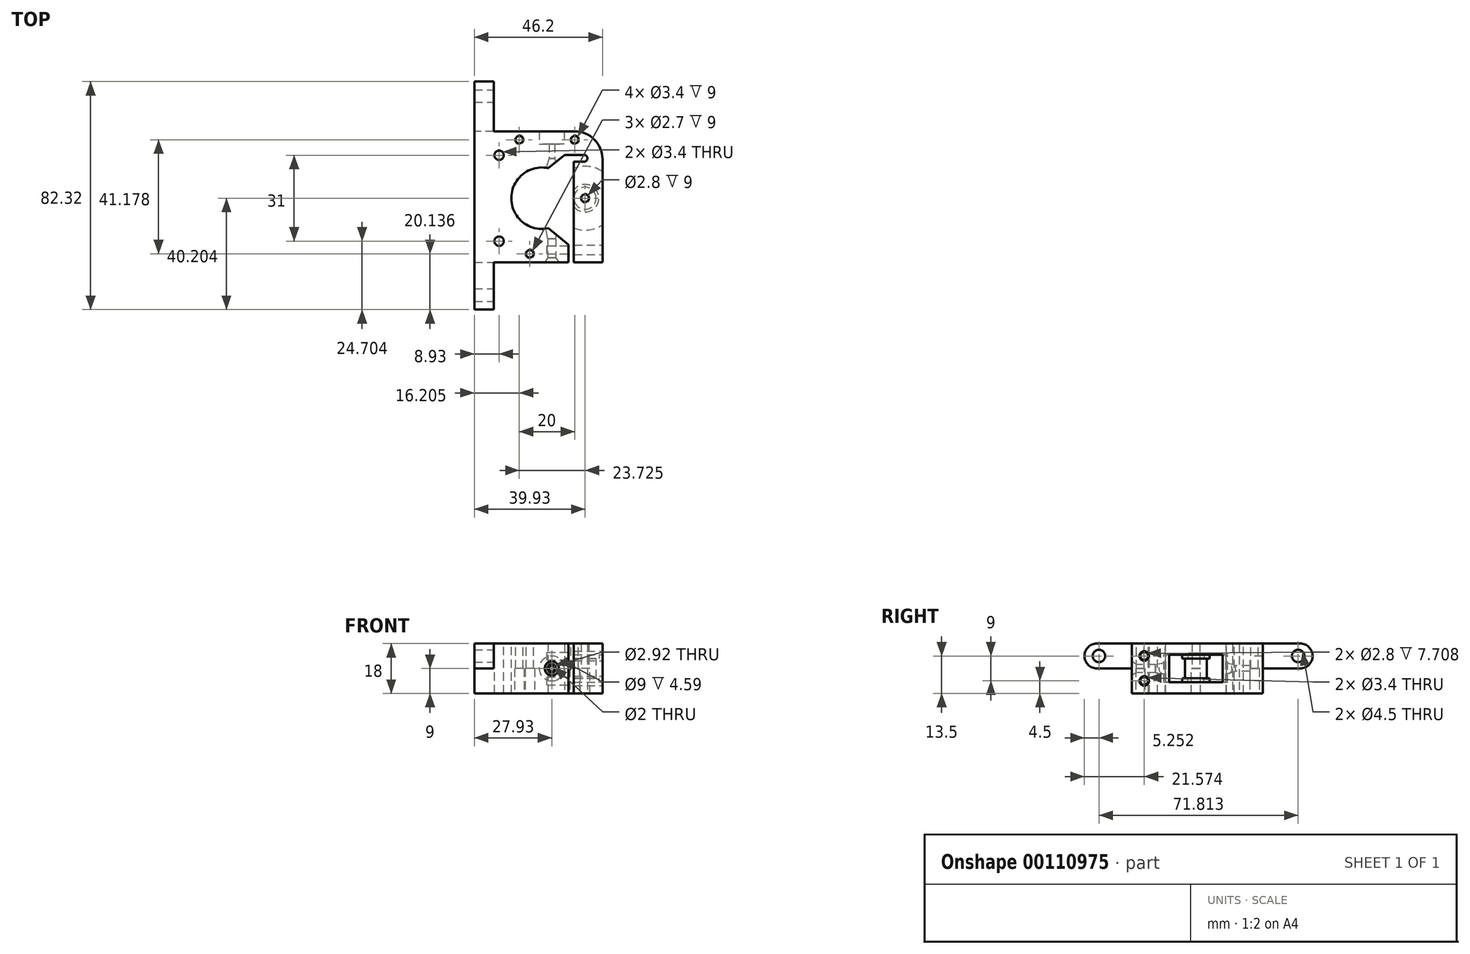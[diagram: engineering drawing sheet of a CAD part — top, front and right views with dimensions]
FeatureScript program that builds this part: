
annotation { "Feature Type Name" : "Feature", "Feature Type Description" : "" }
export const myFeature = defineFeature(function(context is Context, id is Id, definition is map)
    precondition{}
    {
        {
            var Q0;
            Q0=qCreatedBy(makeId("Top.planeOp"),FACE);
            var sketch = newSketch(context, id + "F0", { "sketchPlane" : qUnion([Q0])});
            skLineSegment(sketch, "E0", {"start": v(-24.43, 29.94) * mm, "end": v(-24.43, -17.36) * mm});
            skLineSegment(sketch, "E1", {"start": v(-24.43, -17.36) * mm, "end": v(-24.43, -17.36) * mm});
            skLineSegment(sketch, "E2", {"start": v(-24.43, -17.36) * mm, "end": v(-24.43, -17.35) * mm});
            skLineSegment(sketch, "E3", {"start": v(-24.43, -17.35) * mm, "end": v(9.48, -17.35) * mm});
            skLineSegment(sketch, "E4", {"start": v(9.48, -17.35) * mm, "end": v(9.48, 21.46) * mm});
            skLineSegment(sketch, "E5", {"start": v(9.48, 21.46) * mm, "end": v(15.14, 21.46) * mm});
            skLineSegment(sketch, "E6", {"start": v(15.14, 19) * mm, "end": v(11.48, 19) * mm});
            skLineSegment(sketch, "E7", {"start": v(11.48, 19) * mm, "end": v(11.48, -17.35) * mm});
            skLineSegment(sketch, "E8", {"start": v(11.48, -17.35) * mm, "end": v(21.77, -17.35) * mm});
            skLineSegment(sketch, "E9", {"start": v(21.77, -17.35) * mm, "end": v(21.77, 29.94) * mm});
            skLineSegment(sketch, "E10", {"start": v(21.77, 29.94) * mm, "end": v(-24.43, 29.94) * mm});
            skCircle(sketch, "E11", {"center": v(-8.23, 26.93) * mm, "radius": 1.35 * mm});
            skCircle(sketch, "E12", {"center": v(11.77, 26.93) * mm, "radius": 1.35 * mm});
            skCircle(sketch, "E13", {"center": v(-4.43, -14.24) * mm, "radius": 1.35 * mm});
            skArc(sketch, "E14", {"start": v(15.14, 19) * mm, "mid": v(16.36, 20.23) * mm, "end": v(15.14, 21.46) * mm});
            skCircle(sketch, "E15", {"center": v(-8.23, 26.93) * mm, "radius": 1.7 * mm});
            skCircle(sketch, "E16", {"center": v(11.77, 26.93) * mm, "radius": 1.7 * mm});
            skCircle(sketch, "E17", {"center": v(-4.43, -14.24) * mm, "radius": 1.7 * mm});
            skSolve(sketch);
        }
        {
            var Q0;
            Q0=makeQuery(id+"F0.imprint","IMPRINT",FACE,{"disambiguationData":[TD([[makeQuery(id+"F0.imprint","IMPRINT",EDGE,{"derivedFrom":sQuery(id+"F0.wireOp",EDGE,"E0")}),1.0]])]});
            extrude(context, id + "F1", {"entities" : qUnion([Q0]), "depth" : 9 * mm});
        }
        {
            var Q0;
            Q0=makeQuery(id+"F1.opExtrude","CAP_FACE",FACE,{"disambiguationData":[OSD([sQuery(id+"F0.wireOp",EDGE,"E0"),sQuery(id+"F0.wireOp",EDGE,"E1"),sQuery(id+"F0.wireOp",EDGE,"E2"),sQuery(id+"F0.wireOp",EDGE,"E3"),sQuery(id+"F0.wireOp",EDGE,"E4"),sQuery(id+"F0.wireOp",EDGE,"E5"),sQuery(id+"F0.wireOp",EDGE,"E6"),sQuery(id+"F0.wireOp",EDGE,"E7"),sQuery(id+"F0.wireOp",EDGE,"E8"),sQuery(id+"F0.wireOp",EDGE,"E9"),sQuery(id+"F0.wireOp",EDGE,"E10"),sQuery(id+"F0.wireOp",EDGE,"604cad85-587a-4b7d-8070-06f4cba85480"),sQuery(id+"F0.wireOp",EDGE,"6e5e38c1-5bff-4efe-a8c5-b84022f0a049"),sQuery(id+"F0.wireOp",EDGE,"b8144507-9dd7-4af4-87a3-7b649dd00ae6"),sQuery(id+"F0.wireOp",EDGE,"b9c2cb7c-5e58-4995-888e-a78f0403fbb5"),sQuery(id+"F0.wireOp",EDGE,"885990ab-7576-4c23-8475-595d2769e284"),sQuery(id+"F0.wireOp",EDGE,"E11"),sQuery(id+"F0.wireOp",EDGE,"E12"),sQuery(id+"F0.wireOp",EDGE,"E13"),sQuery(id+"F0.wireOp",EDGE,"E14")])],"isStart":false});
            var sketch = newSketch(context, id + "F2", { "sketchPlane" : qUnion([Q0])});
            skCircle(sketch, "E18", {"center": v(0, 5.82) * mm, "radius": 11.1 * mm});
            skCircle(sketch, "E19", {"center": v(-15.5, 21.32) * mm, "radius": 1.7 * mm});
            skCircle(sketch, "E20", {"center": v(-15.5, -9.68) * mm, "radius": 1.7 * mm});
            skSolve(sketch);
        }
        {
            var Q0;
            Q0=qSketchRegion(id+"F2",true);
            extrude(context, id + "F3", {"entities" : qUnion([Q0]), "operationType" : NewBodyOperationType.REMOVE, "endBound" : BoundingType.THROUGH_ALL, "oppositeDirection" : true, "depth" : 25 * mm});
        }
        {
            var Q0;
            Q0=makeQuery(id+"F1.opExtrude","CAP_FACE",FACE,{"disambiguationData":[OSD([sQuery(id+"F0.wireOp",EDGE,"E0"),sQuery(id+"F0.wireOp",EDGE,"E1"),sQuery(id+"F0.wireOp",EDGE,"E2"),sQuery(id+"F0.wireOp",EDGE,"E3"),sQuery(id+"F0.wireOp",EDGE,"E4"),sQuery(id+"F0.wireOp",EDGE,"E5"),sQuery(id+"F0.wireOp",EDGE,"E6"),sQuery(id+"F0.wireOp",EDGE,"E7"),sQuery(id+"F0.wireOp",EDGE,"E8"),sQuery(id+"F0.wireOp",EDGE,"E9"),sQuery(id+"F0.wireOp",EDGE,"E10"),sQuery(id+"F0.wireOp",EDGE,"604cad85-587a-4b7d-8070-06f4cba85480"),sQuery(id+"F0.wireOp",EDGE,"6e5e38c1-5bff-4efe-a8c5-b84022f0a049"),sQuery(id+"F0.wireOp",EDGE,"E11"),sQuery(id+"F0.wireOp",EDGE,"E12"),sQuery(id+"F0.wireOp",EDGE,"E13"),sQuery(id+"F0.wireOp",EDGE,"E14")])],"isStart":false});
            var sketch = newSketch(context, id + "F4", { "sketchPlane" : qUnion([Q0])});
            skCircle(sketch, "E21", {"center": v(15.5, 5.82) * mm, "radius": 11.5 * mm});
            skCircle(sketch, "E22", {"center": v(15.5, 5.82) * mm, "radius": 5 * mm});
            skCircle(sketch, "E23", {"center": v(15.5, 5.82) * mm, "radius": 4 * mm});
            skLineSegment(sketch, "E24", {"start": v(0, 5.82) * mm, "end": v(31, 5.82) * mm, "construction": true});
            skCircle(sketch, "E25", {"center": v(15.5, 5.82) * mm, "radius": 1.4 * mm});
            skCircle(sketch, "E26", {"center": v(15.5, 5.82) * mm, "radius": 1.7 * mm});
            skSolve(sketch);
        }
        {
            var Q0;
            Q0=makeQuery(id+"F4.imprint","IMPRINT",FACE,{"disambiguationData":[TD([[makeQuery(id+"F4.imprint","IMPRINT",EDGE,{"derivedFrom":sQuery(id+"F4.wireOp",EDGE,"E22")}),-1.0]])]});
            extrude(context, id + "F5", {"entities" : qUnion([Q0]), "operationType" : NewBodyOperationType.REMOVE, "oppositeDirection" : true, "depth" : 5 * mm});
        }
        {
            var Q0;
            Q0=makeQuery(id+"F4.imprint","IMPRINT",FACE,{"disambiguationData":[TD([[makeQuery(id+"F4.imprint","IMPRINT",EDGE,{"derivedFrom":sQuery(id+"F4.wireOp",EDGE,"E22")}),1.0]])]});
            var Q1;
            Q1=makeQuery(id+"F4.imprint","IMPRINT",FACE,{"disambiguationData":[TD([[makeQuery(id+"F4.imprint","IMPRINT",EDGE,{"derivedFrom":sQuery(id+"F4.wireOp",EDGE,"E23")}),-1.0]])]});
            extrude(context, id + "F6", {"entities" : qUnion([Q0, Q1]), "operationType" : NewBodyOperationType.REMOVE, "oppositeDirection" : true, "depth" : 3.5 * mm});
        }
        {
            var Q0;
            {var subQ0=sQuery(id+"F0.wireOp",EDGE,"E0");var subQ1=sQuery(id+"F0.wireOp",EDGE,"E1");var subQ2=sQuery(id+"F0.wireOp",EDGE,"E2");var subQ3=sQuery(id+"F0.wireOp",EDGE,"E3");var subQ4=sQuery(id+"F0.wireOp",EDGE,"E4");var subQ5=sQuery(id+"F0.wireOp",EDGE,"E5");var subQ6=sQuery(id+"F0.wireOp",EDGE,"E6");var subQ7=sQuery(id+"F0.wireOp",EDGE,"E7");var subQ8=sQuery(id+"F0.wireOp",EDGE,"E9");var subQ9=sQuery(id+"F0.wireOp",EDGE,"E10");var subQ10=sQuery(id+"F0.wireOp",EDGE,"604cad85-587a-4b7d-8070-06f4cba85480");var subQ11=sQuery(id+"F0.wireOp",EDGE,"6e5e38c1-5bff-4efe-a8c5-b84022f0a049");var subQ12=sQuery(id+"F0.wireOp",EDGE,"E11");var subQ13=sQuery(id+"F0.wireOp",EDGE,"E12");var subQ14=sQuery(id+"F0.wireOp",EDGE,"E13");var subQ15=sQuery(id+"F0.wireOp",EDGE,"E14");Q0=makeQuery(id+"F5.boolean.opBoolean","SPLIT",FACE,{"disambiguationData":[TD([makeQuery(id+"F1.opExtrude","SWEPT_FACE",FACE,{"disambiguationData":[OSD([subQ0])]})])],"derivedFrom":makeQuery(id+"F1.opExtrude","CAP_FACE",FACE,{"disambiguationData":[OSD([subQ0,subQ1,subQ2,subQ3,subQ4,subQ5,subQ6,subQ7,sQuery(id+"F0.wireOp",EDGE,"E8"),subQ8,subQ9,subQ10,subQ11,subQ12,subQ13,subQ14,subQ15])],"isStart":false})});}
            var sketch = newSketch(context, id + "F7", { "sketchPlane" : qUnion([Q0])});
            skLineSegment(sketch, "E27", {"start": v(-1, 30.34) * mm, "end": v(-1, 25.34) * mm});
            skLineSegment(sketch, "E28", {"start": v(-1, 25.34) * mm, "end": v(2.5, 25.34) * mm});
            skLineSegment(sketch, "E29", {"start": v(2.5, 25.34) * mm, "end": v(2.5, 20.21) * mm});
            skLineSegment(sketch, "E30", {"start": v(2.5, 20.21) * mm, "end": v(0.95, 15.18) * mm});
            skLineSegment(sketch, "E31", {"start": v(0.95, 15.18) * mm, "end": v(3.5, 15.18) * mm});
            skLineSegment(sketch, "E32", {"start": v(3.5, 15.18) * mm, "end": v(3.5, 30.34) * mm});
            skLineSegment(sketch, "E33", {"start": v(3.5, 30.34) * mm, "end": v(-1, 30.34) * mm});
            skLineSegment(sketch, "E34", {"start": v(3.5, -3.13) * mm, "end": v(3.5, -17.35) * mm});
            skLineSegment(sketch, "E35", {"start": v(0.95, -3.15) * mm, "end": v(2.04, -8.75) * mm});
            skLineSegment(sketch, "E36", {"start": v(2.04, -8.75) * mm, "end": v(2.04, -15.66) * mm});
            skLineSegment(sketch, "E37", {"start": v(2.04, -15.66) * mm, "end": v(0.95, -17.35) * mm});
            skLineSegment(sketch, "E38", {"start": v(0.95, -3.15) * mm, "end": v(3.5, -3.13) * mm});
            skSolve(sketch);
        }
        {
            var Q0;
            Q0=qSketchRegion(id+"F7",true);
            var Q1;
            {var subQ1=sQuery(id+"F7.wireOp",EDGE,"E34");Q1=makeQuery(id+"F7.imprint","IMPRINT",FACE,{"disambiguationData":[TD([[makeQuery(id+"F7.imprint","IMPRINT",EDGE,{"derivedFrom":subQ1}),-1.0]])]});}
            var Q2;
            {var subQ0=sQuery(id+"F7.wireOp",EDGE,"E38");Q2=makeQuery(id+"F7.imprint","IMPRINT",FACE,{"disambiguationData":[TD([[makeQuery(id+"F7.imprint","IMPRINT",EDGE,{"derivedFrom":subQ0}),-1.0]])]});}
            var Q3;
            {var subQ6=sQuery(id+"F7.wireOp",EDGE,"E36");Q3=makeQuery(id+"F7.imprint","IMPRINT",FACE,{"disambiguationData":[TD([[makeQuery(id+"F7.imprint","IMPRINT",EDGE,{"derivedFrom":subQ6}),1.0]])]});}
            var Q4;
            Q4=sQuery(id+"F7.wireOp",EDGE,"E32");
            revolve(context, id + "F8", {"entities" : qUnion([Q0, Q1, Q2, Q3]), "axis" : qUnion([Q4]), "revolveType" : RevolveType.FULL});
        }
        {
            var Q0;
            Q0=makeQuery(id+"F8.opRevolve","SWEPT_BODY",BODY,{"disambiguationData":[OSD([sQuery(id+"F7.wireOp",EDGE,"E27"),sQuery(id+"F7.wireOp",EDGE,"E28"),sQuery(id+"F7.wireOp",EDGE,"E29"),sQuery(id+"F7.wireOp",EDGE,"E30"),sQuery(id+"F7.wireOp",EDGE,"E31"),sQuery(id+"F7.wireOp",EDGE,"E32"),sQuery(id+"F7.wireOp",EDGE,"E33")])]});
            var Q1;
            Q1=makeQuery(id+"F8.opRevolve","SWEPT_BODY",BODY,{"disambiguationData":[OSD([sQuery(id+"F0.wireOp",EDGE,"E3"),sQuery(id+"F7.wireOp",EDGE,"E34"),sQuery(id+"F7.wireOp",EDGE,"E35"),sQuery(id+"F7.wireOp",EDGE,"E36"),sQuery(id+"F7.wireOp",EDGE,"E37"),sQuery(id+"F7.wireOp",EDGE,"E38")])]});
            var Q2;
            Q2=makeQuery(id+"F1.opExtrude","SWEPT_BODY",BODY,{"disambiguationData":[OSD([sQuery(id+"F0.wireOp",EDGE,"E0"),sQuery(id+"F0.wireOp",EDGE,"E1"),sQuery(id+"F0.wireOp",EDGE,"E2"),sQuery(id+"F0.wireOp",EDGE,"E3"),sQuery(id+"F0.wireOp",EDGE,"E4"),sQuery(id+"F0.wireOp",EDGE,"E5"),sQuery(id+"F0.wireOp",EDGE,"E6"),sQuery(id+"F0.wireOp",EDGE,"E7"),sQuery(id+"F0.wireOp",EDGE,"E8"),sQuery(id+"F0.wireOp",EDGE,"E9"),sQuery(id+"F0.wireOp",EDGE,"E10"),sQuery(id+"F0.wireOp",EDGE,"604cad85-587a-4b7d-8070-06f4cba85480"),sQuery(id+"F0.wireOp",EDGE,"6e5e38c1-5bff-4efe-a8c5-b84022f0a049"),sQuery(id+"F0.wireOp",EDGE,"E11"),sQuery(id+"F0.wireOp",EDGE,"E12"),sQuery(id+"F0.wireOp",EDGE,"E13"),sQuery(id+"F0.wireOp",EDGE,"E14")])]});
            booleanBodies(context, id + "F9", {"operationType" : BooleanOperationType.SUBTRACTION, "tools" : qUnion([Q0, Q1]), "targets" : qUnion([Q2]), "keepTools" : true});
        }
        {
            var Q0;
            Q0=makeQuery(id+"F8.opRevolve","SWEPT_BODY",BODY,{"disambiguationData":[OSD([sQuery(id+"F7.wireOp",EDGE,"E27"),sQuery(id+"F7.wireOp",EDGE,"E28"),sQuery(id+"F7.wireOp",EDGE,"E29"),sQuery(id+"F7.wireOp",EDGE,"E30"),sQuery(id+"F7.wireOp",EDGE,"E31"),sQuery(id+"F7.wireOp",EDGE,"E32"),sQuery(id+"F7.wireOp",EDGE,"E33")])]});
            var Q1;
            Q1=makeQuery(id+"F8.opRevolve","SWEPT_BODY",BODY,{"disambiguationData":[OSD([sQuery(id+"F0.wireOp",EDGE,"E3"),sQuery(id+"F7.wireOp",EDGE,"E34"),sQuery(id+"F7.wireOp",EDGE,"E35"),sQuery(id+"F7.wireOp",EDGE,"E36"),sQuery(id+"F7.wireOp",EDGE,"E37"),sQuery(id+"F7.wireOp",EDGE,"E38")])]});
            var Q2;
            Q2=makeQuery(id+"F1.opExtrude","SWEPT_BODY",BODY,{"disambiguationData":[OSD([sQuery(id+"F0.wireOp",EDGE,"E0"),sQuery(id+"F0.wireOp",EDGE,"E1"),sQuery(id+"F0.wireOp",EDGE,"E2"),sQuery(id+"F0.wireOp",EDGE,"E3"),sQuery(id+"F0.wireOp",EDGE,"E4"),sQuery(id+"F0.wireOp",EDGE,"E5"),sQuery(id+"F0.wireOp",EDGE,"E6"),sQuery(id+"F0.wireOp",EDGE,"E7"),sQuery(id+"F0.wireOp",EDGE,"E8"),sQuery(id+"F0.wireOp",EDGE,"E9"),sQuery(id+"F0.wireOp",EDGE,"E10"),sQuery(id+"F0.wireOp",EDGE,"604cad85-587a-4b7d-8070-06f4cba85480"),sQuery(id+"F0.wireOp",EDGE,"6e5e38c1-5bff-4efe-a8c5-b84022f0a049"),sQuery(id+"F0.wireOp",EDGE,"E11"),sQuery(id+"F0.wireOp",EDGE,"E12"),sQuery(id+"F0.wireOp",EDGE,"E13"),sQuery(id+"F0.wireOp",EDGE,"E14")])]});
            booleanBodies(context, id + "F10", {"operationType" : BooleanOperationType.SUBTRACTION, "tools" : qUnion([Q0, Q1]), "targets" : qUnion([Q2]), "keepTools" : true});
        }
        {
            var Q0;
            Q0=makeQuery(id+"F1.opExtrude","SWEPT_EDGE",EDGE,{"disambiguationData":[OSD([sQuery(id+"F0.wireOp",EDGE,"E9"),sQuery(id+"F0.wireOp",EDGE,"E10")])]});
            fillet(context, id + "F11", {"entities" : qUnion([Q0]), "radius" : 10 * mm, "tangentPropagation" : true, "allowEdgeOverflow" : false});
        }
        {
            var Q0;
            Q0=qSketchRegion(id+"F0",true);
            var Q1;
            Q1=makeQuery(id+"F0.imprint","IMPRINT",FACE,{"disambiguationData":[TD([[makeQuery(id+"F0.imprint","IMPRINT",EDGE,{"derivedFrom":sQuery(id+"F0.wireOp",EDGE,"E12")}),-1.0]])]});
            var Q2;
            Q2=makeQuery(id+"F0.imprint","IMPRINT",FACE,{"disambiguationData":[TD([[makeQuery(id+"F0.imprint","IMPRINT",EDGE,{"derivedFrom":sQuery(id+"F0.wireOp",EDGE,"E11")}),-1.0]])]});
            var Q3;
            Q3=makeQuery(id+"F0.imprint","IMPRINT",FACE,{"disambiguationData":[TD([[makeQuery(id+"F0.imprint","IMPRINT",EDGE,{"derivedFrom":sQuery(id+"F0.wireOp",EDGE,"E13")}),-1.0]])]});
            extrude(context, id + "F12", {"entities" : qUnion([Q0, Q1, Q2, Q3]), "oppositeDirection" : true, "depth" : 9 * mm});
        }
        {
            var Q0;
            Q0=makeQuery(id+"F12.opExtrude","SWEPT_BODY",BODY,{"disambiguationData":[OSD([sQuery(id+"F0.wireOp",EDGE,"E0"),sQuery(id+"F0.wireOp",EDGE,"E3"),sQuery(id+"F0.wireOp",EDGE,"E4"),sQuery(id+"F0.wireOp",EDGE,"E5"),sQuery(id+"F0.wireOp",EDGE,"E6"),sQuery(id+"F0.wireOp",EDGE,"E7"),sQuery(id+"F0.wireOp",EDGE,"E8"),sQuery(id+"F0.wireOp",EDGE,"E9"),sQuery(id+"F0.wireOp",EDGE,"E10"),sQuery(id+"F0.wireOp",EDGE,"E11"),sQuery(id+"F0.wireOp",EDGE,"E12"),sQuery(id+"F0.wireOp",EDGE,"E13"),sQuery(id+"F0.wireOp",EDGE,"E14")])]});
            transform(context, id + "F13", {"entities" : qUnion([Q0]), "transformType" : TransformType.TRANSLATION_3D, "dx" : 0 * mm, "dy" : 0 * mm, "dz" : 18 * mm, "makeCopy" : false});
        }
        {
            var Q0;
            Q0=makeQuery(id+"F12.opExtrude","SWEPT_EDGE",EDGE,{"disambiguationData":[OSD([sQuery(id+"F0.wireOp",EDGE,"E9"),sQuery(id+"F0.wireOp",EDGE,"E10")])]});
            fillet(context, id + "F14", {"entities" : qUnion([Q0]), "radius" : 10 * mm, "tangentPropagation" : true, "allowEdgeOverflow" : false});
        }
        {
            var Q0;
            Q0=qSketchRegion(id+"F2",true);
            extrude(context, id + "F15", {"entities" : qUnion([Q0]), "operationType" : NewBodyOperationType.REMOVE, "endBound" : BoundingType.THROUGH_ALL, "depth" : 25 * mm});
        }
        {
            var Q0;
            {var subQ3=sQuery(id+"F4.wireOp",EDGE,"E21");var subQ7=makeQuery(id+"F1.opExtrude","CAP_EDGE",EDGE,{"disambiguationData":[OSD([sQuery(id+"F0.wireOp",EDGE,"E9")])],"isStart":false});var subQ9=makeQuery(id+"F4.imprint","INTERSECT",VERTEX,{"disambiguationData":[OD(0.0)],"derivedFrom":[subQ7,subQ3]});Q0=makeQuery(id+"F4.imprint","IMPRINT",FACE,{"disambiguationData":[TD([[makeQuery(id+"F4.imprint","IMPRINT",EDGE,{"disambiguationData":[TD([[subQ9,-1.0]])],"derivedFrom":subQ3}),1.0]])]});}
            extrude(context, id + "F16", {"entities" : qUnion([Q0]), "operationType" : NewBodyOperationType.REMOVE, "depth" : 5 * mm});
        }
        {
            var Q0;
            Q0=makeQuery(id+"F4.imprint","IMPRINT",FACE,{"disambiguationData":[TD([[makeQuery(id+"F4.imprint","IMPRINT",EDGE,{"derivedFrom":sQuery(id+"F4.wireOp",EDGE,"E23")}),-1.0]])]});
            extrude(context, id + "F17", {"entities" : qUnion([Q0]), "operationType" : NewBodyOperationType.REMOVE, "depth" : 3.5 * mm});
        }
        {
            var Q0;
            Q0=makeQuery(id+"F8.opRevolve","SWEPT_BODY",BODY,{"disambiguationData":[OSD([sQuery(id+"F7.wireOp",EDGE,"E27"),sQuery(id+"F7.wireOp",EDGE,"E28"),sQuery(id+"F7.wireOp",EDGE,"E29"),sQuery(id+"F7.wireOp",EDGE,"E30"),sQuery(id+"F7.wireOp",EDGE,"E31"),sQuery(id+"F7.wireOp",EDGE,"E32"),sQuery(id+"F7.wireOp",EDGE,"E33")])]});
            var Q1;
            Q1=makeQuery(id+"F12.opExtrude","SWEPT_BODY",BODY,{"disambiguationData":[OSD([sQuery(id+"F0.wireOp",EDGE,"E0"),sQuery(id+"F0.wireOp",EDGE,"E3"),sQuery(id+"F0.wireOp",EDGE,"E4"),sQuery(id+"F0.wireOp",EDGE,"E5"),sQuery(id+"F0.wireOp",EDGE,"E6"),sQuery(id+"F0.wireOp",EDGE,"E7"),sQuery(id+"F0.wireOp",EDGE,"E8"),sQuery(id+"F0.wireOp",EDGE,"E9"),sQuery(id+"F0.wireOp",EDGE,"E10"),sQuery(id+"F0.wireOp",EDGE,"E11"),sQuery(id+"F0.wireOp",EDGE,"E12"),sQuery(id+"F0.wireOp",EDGE,"E13"),sQuery(id+"F0.wireOp",EDGE,"E14")])]});
            booleanBodies(context, id + "F18", {"operationType" : BooleanOperationType.SUBTRACTION, "tools" : qUnion([Q0]), "targets" : qUnion([Q1])});
        }
        {
            var Q0;
            Q0=makeQuery(id+"F8.opRevolve","SWEPT_BODY",BODY,{"disambiguationData":[OSD([sQuery(id+"F0.wireOp",EDGE,"E3"),sQuery(id+"F7.wireOp",EDGE,"E34"),sQuery(id+"F7.wireOp",EDGE,"E35"),sQuery(id+"F7.wireOp",EDGE,"E36"),sQuery(id+"F7.wireOp",EDGE,"E37"),sQuery(id+"F7.wireOp",EDGE,"E38")])]});
            var Q1;
            Q1=makeQuery(id+"F12.opExtrude","SWEPT_BODY",BODY,{"disambiguationData":[OSD([sQuery(id+"F0.wireOp",EDGE,"E0"),sQuery(id+"F0.wireOp",EDGE,"E3"),sQuery(id+"F0.wireOp",EDGE,"E4"),sQuery(id+"F0.wireOp",EDGE,"E5"),sQuery(id+"F0.wireOp",EDGE,"E6"),sQuery(id+"F0.wireOp",EDGE,"E7"),sQuery(id+"F0.wireOp",EDGE,"E8"),sQuery(id+"F0.wireOp",EDGE,"E9"),sQuery(id+"F0.wireOp",EDGE,"E10"),sQuery(id+"F0.wireOp",EDGE,"E11"),sQuery(id+"F0.wireOp",EDGE,"E12"),sQuery(id+"F0.wireOp",EDGE,"E13"),sQuery(id+"F0.wireOp",EDGE,"E14")])]});
            booleanBodies(context, id + "F19", {"operationType" : BooleanOperationType.SUBTRACTION, "tools" : qUnion([Q0]), "targets" : qUnion([Q1])});
        }
        {
            var Q0;
            Q0=makeQuery(id+"F12.opExtrude","SWEPT_FACE",FACE,{"disambiguationData":[OSD([sQuery(id+"F0.wireOp",EDGE,"E9")])]});
            var sketch = newSketch(context, id + "F20", { "sketchPlane" : qUnion([Q0])});
            skCircle(sketch, "E39", {"center": v(-12.8, 13.5) * mm, "radius": 1.7 * mm});
            skCircle(sketch, "E40", {"center": v(-12.8, 13.5) * mm, "radius": 1.4 * mm});
            skCircle(sketch, "E41", {"center": v(-12.8, 4.5) * mm, "radius": 1.7 * mm});
            skCircle(sketch, "E42", {"center": v(-12.8, 4.5) * mm, "radius": 1.4 * mm});
            skSolve(sketch);
        }
        {
            var Q0;
            Q0=makeQuery(id+"F20.imprint","IMPRINT",FACE,{"disambiguationData":[TD([[makeQuery(id+"F20.imprint","IMPRINT",EDGE,{"derivedFrom":sQuery(id+"F20.wireOp",EDGE,"E40")}),1.0]])]});
            extrude(context, id + "F21", {"entities" : qUnion([Q0]), "operationType" : NewBodyOperationType.REMOVE, "oppositeDirection" : true, "depth" : 20 * mm});
        }
        {
            var Q0;
            Q0=makeQuery(id+"F20.imprint","IMPRINT",FACE,{"disambiguationData":[TD([[makeQuery(id+"F20.imprint","IMPRINT",EDGE,{"derivedFrom":sQuery(id+"F20.wireOp",EDGE,"E39")}),1.0]])]});
            extrude(context, id + "F22", {"entities" : qUnion([Q0]), "operationType" : NewBodyOperationType.REMOVE, "oppositeDirection" : true, "depth" : 11 * mm});
        }
        {
            var Q0;
            Q0=makeQuery(id+"F20.imprint","IMPRINT",FACE,{"disambiguationData":[TD([[makeQuery(id+"F20.imprint","IMPRINT",EDGE,{"derivedFrom":sQuery(id+"F20.wireOp",EDGE,"E42")}),1.0]])]});
            extrude(context, id + "F23", {"entities" : qUnion([Q0]), "operationType" : NewBodyOperationType.REMOVE, "oppositeDirection" : true, "depth" : 20 * mm});
        }
        {
            var Q0;
            Q0=makeQuery(id+"F20.imprint","IMPRINT",FACE,{"disambiguationData":[TD([[makeQuery(id+"F20.imprint","IMPRINT",EDGE,{"derivedFrom":sQuery(id+"F20.wireOp",EDGE,"E41")}),1.0]])]});
            extrude(context, id + "F24", {"entities" : qUnion([Q0]), "operationType" : NewBodyOperationType.REMOVE, "oppositeDirection" : true, "depth" : 11 * mm});
        }
        {
            var Q0;
            Q0=makeQuery(id+"F4.imprint","IMPRINT",FACE,{"disambiguationData":[TD([[makeQuery(id+"F4.imprint","IMPRINT",EDGE,{"derivedFrom":sQuery(id+"F4.wireOp",EDGE,"E25")}),1.0]])]});
            var Q1;
            Q1=makeQuery(id+"F4.imprint","IMPRINT",FACE,{"disambiguationData":[TD([[makeQuery(id+"F4.imprint","IMPRINT",EDGE,{"derivedFrom":sQuery(id+"F4.wireOp",EDGE,"E25")}),-1.0]])]});
            extrude(context, id + "F25", {"entities" : qUnion([Q0, Q1]), "operationType" : NewBodyOperationType.REMOVE, "oppositeDirection" : true, "depth" : 25 * mm});
        }
        {
            var Q0;
            Q0=makeQuery(id+"F4.imprint","IMPRINT",FACE,{"disambiguationData":[TD([[makeQuery(id+"F4.imprint","IMPRINT",EDGE,{"derivedFrom":sQuery(id+"F4.wireOp",EDGE,"E25")}),1.0]])]});
            extrude(context, id + "F26", {"entities" : qUnion([Q0]), "operationType" : NewBodyOperationType.REMOVE, "depth" : 25 * mm});
        }
        {
            var Q0;
            Q0=makeQuery(id+"F12.opExtrude","SWEPT_FACE",FACE,{"disambiguationData":[OSD([sQuery(id+"F0.wireOp",EDGE,"E10")])]});
            var sketch = newSketch(context, id + "F27", { "sketchPlane" : qUnion([Q0])});
            skLineSegment(sketch, "E43.bottom", {"start": v(24.43, 9) * mm, "end": v(17.43, 9) * mm});
            skLineSegment(sketch, "E43.top", {"start": v(24.43, 18) * mm, "end": v(17.43, 18) * mm});
            skLineSegment(sketch, "E43.left", {"start": v(24.43, 9) * mm, "end": v(24.43, 18) * mm});
            skLineSegment(sketch, "E43.right", {"start": v(17.43, 9) * mm, "end": v(17.43, 18) * mm});
            skSolve(sketch);
        }
        {
            var Q0;
            Q0=qSketchRegion(id+"F27",true);
            extrude(context, id + "F28", {"entities" : qUnion([Q0]), "operationType" : NewBodyOperationType.ADD, "depth" : 18 * mm, "hasSecondDirection" : true, "secondDirectionOppositeDirection" : true, "secondDirectionDepth" : 64.31 * mm});
        }
        {
            var Q0;
            {var subQ0=sQuery(id+"F27.wireOp",EDGE,"E43.right");var subQ3=sQuery(id+"F0.wireOp",EDGE,"E3");Q0=makeQuery(id+"F28.boolean.opBoolean","SPLIT",FACE,{"disambiguationData":[TD([makeQuery(id+"F12.opExtrude","SWEPT_FACE",FACE,{"disambiguationData":[OSD([subQ3])]})])],"derivedFrom":makeQuery(id+"F28.opExtrude","SWEPT_FACE",FACE,{"disambiguationData":[OSD([subQ0])]})});}
            var sketch = newSketch(context, id + "F29", { "sketchPlane" : qUnion([Q0])});
            skCircle(sketch, "E44", {"center": v(-29.13, 13.5) * mm, "radius": 2.25 * mm});
            skPoint(sketch, "E45", {"position": v(-34.38, 13.5) * mm});
            skSolve(sketch);
        }
        {
            var Q0;
            {var subQ0=sQuery(id+"F27.wireOp",EDGE,"E43.right");var subQ3=sQuery(id+"F0.wireOp",EDGE,"E10");Q0=makeQuery(id+"F28.boolean.opBoolean","SPLIT",FACE,{"disambiguationData":[TD([makeQuery(id+"F12.opExtrude","SWEPT_FACE",FACE,{"disambiguationData":[OSD([subQ3])]})])],"derivedFrom":makeQuery(id+"F28.opExtrude","SWEPT_FACE",FACE,{"disambiguationData":[OSD([subQ0])]})});}
            var sketch = newSketch(context, id + "F30", { "sketchPlane" : qUnion([Q0])});
            skCircle(sketch, "E46", {"center": v(42.69, 13.5) * mm, "radius": 2.25 * mm});
            skPoint(sketch, "E47", {"position": v(47.94, 13.5) * mm});
            skSolve(sketch);
        }
        {
            var Q0;
            Q0=qSketchRegion(id+"F29",true);
            var Q1;
            Q1=qSketchRegion(id+"F30",true);
            extrude(context, id + "F31", {"entities" : qUnion([Q0, Q1]), "operationType" : NewBodyOperationType.REMOVE, "oppositeDirection" : true, "depth" : 25 * mm});
        }
        {
            var Q0;
            Q0=makeQuery(id+"F28.opExtrude","CAP_EDGE",EDGE,{"disambiguationData":[OSD([sQuery(id+"F27.wireOp",EDGE,"E43.top")])],"isStart":true});
            var Q1;
            Q1=makeQuery(id+"F28.opExtrude","CAP_EDGE",EDGE,{"disambiguationData":[OSD([sQuery(id+"F27.wireOp",EDGE,"E43.bottom")])],"isStart":true});
            var Q2;
            Q2=makeQuery(id+"F28.opExtrude","CAP_EDGE",EDGE,{"disambiguationData":[OSD([sQuery(id+"F27.wireOp",EDGE,"E43.top")])],"isStart":false});
            var Q3;
            Q3=makeQuery(id+"F28.opExtrude","CAP_EDGE",EDGE,{"disambiguationData":[OSD([sQuery(id+"F27.wireOp",EDGE,"E43.bottom")])],"isStart":false});
            fillet(context, id + "F32", {"entities" : qUnion([Q0, Q1, Q2, Q3]), "radius" : 4.5 * mm, "tangentPropagation" : true, "allowEdgeOverflow" : false});
        }
        {
            var Q0;
            Q0=makeQuery(id+"F3.boolean.opBoolean","INTERSECT",EDGE,{"disambiguationData":[OD(0.0)],"derivedFrom":[makeQuery(id+"F1.opExtrude","SWEPT_FACE",FACE,{"disambiguationData":[OSD([sQuery(id+"F0.wireOp",EDGE,"E4")])]}),makeQuery(id+"F3.opExtrude","SWEPT_FACE",FACE,{"disambiguationData":[OSD([sQuery(id+"F2.wireOp",EDGE,"E18")])]})]});
            var Q1;
            Q1=makeQuery(id+"F3.boolean.opBoolean","INTERSECT",EDGE,{"disambiguationData":[OD(1.0)],"derivedFrom":[makeQuery(id+"F1.opExtrude","SWEPT_FACE",FACE,{"disambiguationData":[OSD([sQuery(id+"F0.wireOp",EDGE,"E4")])]}),makeQuery(id+"F3.opExtrude","SWEPT_FACE",FACE,{"disambiguationData":[OSD([sQuery(id+"F2.wireOp",EDGE,"E18")])]})]});
            var Q2;
            Q2=makeQuery(id+"F15.boolean.opBoolean","INTERSECT",EDGE,{"disambiguationData":[OD(1.0)],"derivedFrom":[makeQuery(id+"F12.opExtrude","SWEPT_FACE",FACE,{"disambiguationData":[OSD([sQuery(id+"F0.wireOp",EDGE,"E4")])]}),makeQuery(id+"F15.opExtrude","SWEPT_FACE",FACE,{"disambiguationData":[OSD([sQuery(id+"F2.wireOp",EDGE,"E18")])]})]});
            var Q3;
            Q3=makeQuery(id+"F15.boolean.opBoolean","INTERSECT",EDGE,{"disambiguationData":[OD(0.0)],"derivedFrom":[makeQuery(id+"F12.opExtrude","SWEPT_FACE",FACE,{"disambiguationData":[OSD([sQuery(id+"F0.wireOp",EDGE,"E4")])]}),makeQuery(id+"F15.opExtrude","SWEPT_FACE",FACE,{"disambiguationData":[OSD([sQuery(id+"F2.wireOp",EDGE,"E18")])]})]});
            chamfer(context, id + "F33", {"entities" : qUnion([Q0, Q1, Q2, Q3]), "width" : 6 * mm, "tangentPropagation" : true});
        }
    });
